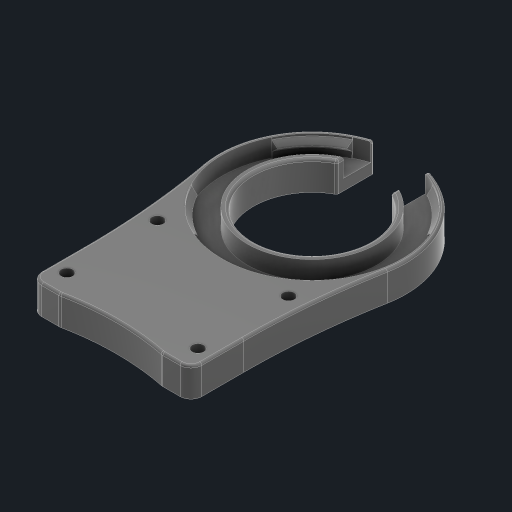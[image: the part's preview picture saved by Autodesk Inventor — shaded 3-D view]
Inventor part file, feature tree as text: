
AUTODESK INVENTOR PART (.ipt)
format: ipt  version: 2023 (Build 270158000, 158)  size: 369,664 bytes
history: native  units: mm
features: extrude x7, fillet x7, sketch x5, draft x2, revolve x1, direct_edit x1, other x1
ambient origin geometry x8: Origin, YZ Plane, XZ Plane, XY Plane, X Axis, Y Axis, Z Axis, Center Point
bodies: Solid1 (feature_tree)
feature tree (24):
  sketch  "Sketch1"  dims[d0=35.5mm d2=49.02mm]
  extrude  "Extrusion1"  Depth=49.02mm
  extrude  "Extrusion2"  Depth=7.0mm TaperAngle=0.0deg
  draft  "FaceDraft1"
  sketch  "Sketch2"  dims[d3=1.2mm d4=7.0mm d5=0.0mm]
  extrude  "Extrusion3"  Depth=0.401426mm
  revolve  "Revolution1"  [1 undecoded]
  extrude  "Extrusion4"  Depth=6.0mm TaperAngle=0.0deg
  direct_edit  "Direct Edit3"
  extrude  "Extrusion6"  Depth=3.1mm
  extrude  "Extrusion7"  Depth=3.0mm
  fillet  "Fillet5"  [1 undecoded]
  fillet  "Fillet6"  [1 undecoded]
  extrude  "Extrusion8"  Depth=23.1mm
  fillet  "Fillet7"  [1 undecoded]
  draft  "FaceDraft3"
  fillet  "Fillet8"  [1 undecoded]
  fillet  "Fillet9"  Radius=14.9mm
  fillet  "Fillet10"  [1 undecoded]
  fillet  "Fillet11"  Radius=3.0mm
  sketch  "Sketch3"  dims[d6=2.0mm d7=0.0mm d8=0.401426mm]
  sketch  "Sketch5"  dims[d22=1.6mm d23=14.9mm]
  sketch  "Sketch6"  dims[d24=3.0mm d25=6.0mm d26=0.0mm d29=3.1mm d30=3.0mm d31=45.0deg d32=90.0deg d33=23.1mm d34=90.0deg d35=0.0mm d36=0.0mm d40=14.9mm d49=-0.127mm d51=3.0mm d52=0.0mm d53=22.0mm d54=22.0mm d55=10.0mm d56=0.0mm d57=0.8mm d58=0.5mm d59=45.0mm d60=8.0mm d61=14.0mm d62=42.0mm d63=3.0mm d64=0.0mm d65=0.7mm d66=3.2mm d67=24.5mm d68=3.2mm d69=24.9mm d70=1.745329mm d71=70.0mm d72=200.0mm d73=3.0mm d74=0.6mm]
  other  "Size1"
note: 6 required parameter values undecoded (feature->parameter linkage not recoverable at this tier; creation-order binding heuristic only, values carry confidence <= 0.55)